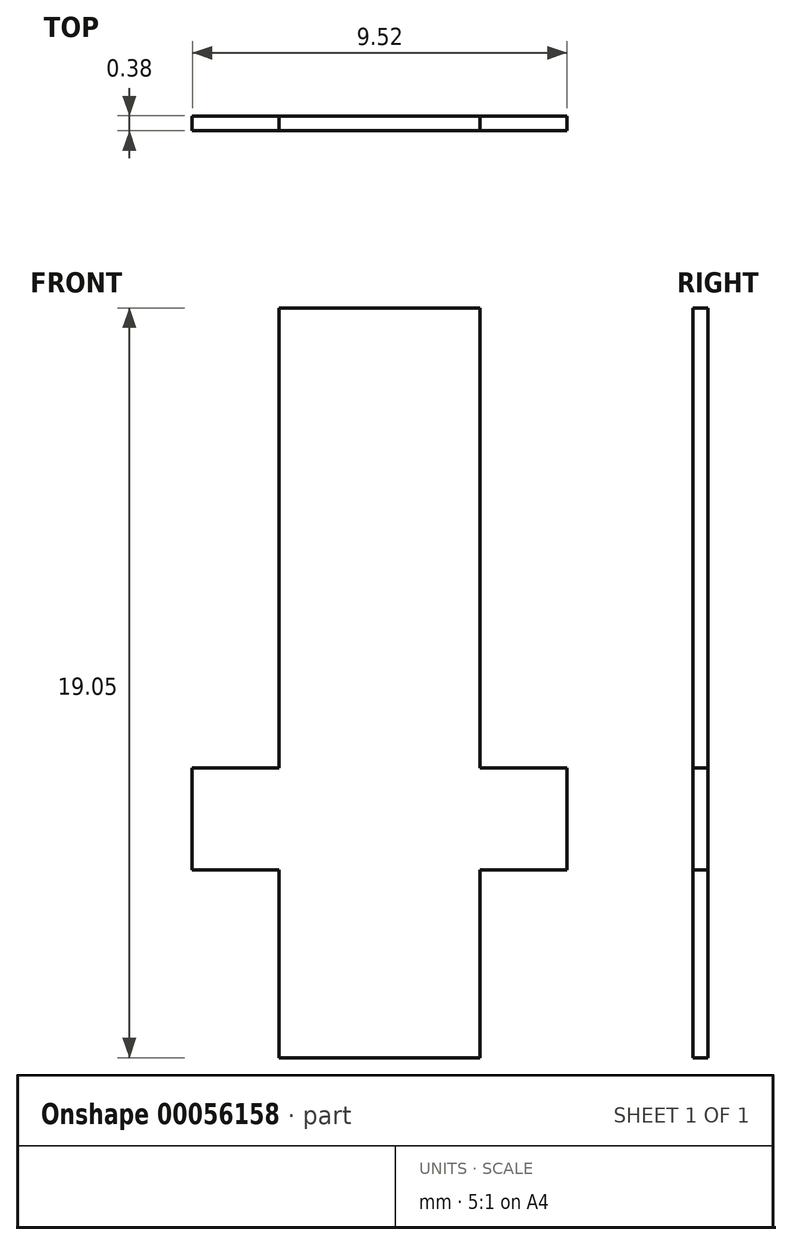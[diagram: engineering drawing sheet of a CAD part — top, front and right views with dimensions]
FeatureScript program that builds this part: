
annotation { "Feature Type Name" : "Feature", "Feature Type Description" : "" }
export const myFeature = defineFeature(function(context is Context, id is Id, definition is map)
    precondition{}
    {
        {
            assignVariable(context, id + "F0", {"name" : "thick", "anyValue" : .188});
        }
        {
            var Q0;
            Q0=qCreatedBy(makeId("Front.planeOp"),FACE);
            var sketch = newSketch(context, id + "F1", { "sketchPlane" : qUnion([Q0])});
            skLineSegment(sketch, "E0", {"start": v(-2.55, 0) * mm, "end": v(-2.55, 11.69) * mm});
            skLineSegment(sketch, "E1", {"start": v(-2.55, 11.69) * mm, "end": v(2.55, 11.69) * mm});
            skLineSegment(sketch, "E2", {"start": v(2.55, 11.69) * mm, "end": v(2.55, 0) * mm});
            skLineSegment(sketch, "E3", {"start": v(2.55, 0) * mm, "end": v(4.76, 0) * mm});
            skLineSegment(sketch, "E4", {"start": v(4.76, 0) * mm, "end": v(4.76, -2.59) * mm});
            skLineSegment(sketch, "E5", {"start": v(4.76, -2.59) * mm, "end": v(2.55, -2.59) * mm});
            skLineSegment(sketch, "E6", {"start": v(2.55, -2.59) * mm, "end": v(2.55, -7.36) * mm});
            skLineSegment(sketch, "E7", {"start": v(2.55, -7.36) * mm, "end": v(-2.55, -7.36) * mm});
            skLineSegment(sketch, "E8", {"start": v(-2.55, -7.36) * mm, "end": v(-2.55, -2.59) * mm});
            skLineSegment(sketch, "E9", {"start": v(-2.55, -2.59) * mm, "end": v(-4.76, -2.59) * mm});
            skLineSegment(sketch, "E10", {"start": v(-4.76, -2.59) * mm, "end": v(-4.76, 0) * mm});
            skLineSegment(sketch, "E11", {"start": v(-4.76, 0) * mm, "end": v(-2.55, 0) * mm});
            skLineSegment(sketch, "E12", {"start": v(-2.55, 0) * mm, "end": v(0, 0) * mm, "construction": true});
            skLineSegment(sketch, "E13", {"start": v(2.55, 0) * mm, "end": v(0, 0) * mm, "construction": true});
            skSolve(sketch);
        }
        {
            var Q0;
            Q0 = qSketchRegion(id + "F1", true);
            extrude(context, id + "F2", {"entities" : qUnion([Q0]), "endBound" : BoundingType.SYMMETRIC, "depth" : (getVariable(context, 'thick') * 2) * mm});
        }
    });
